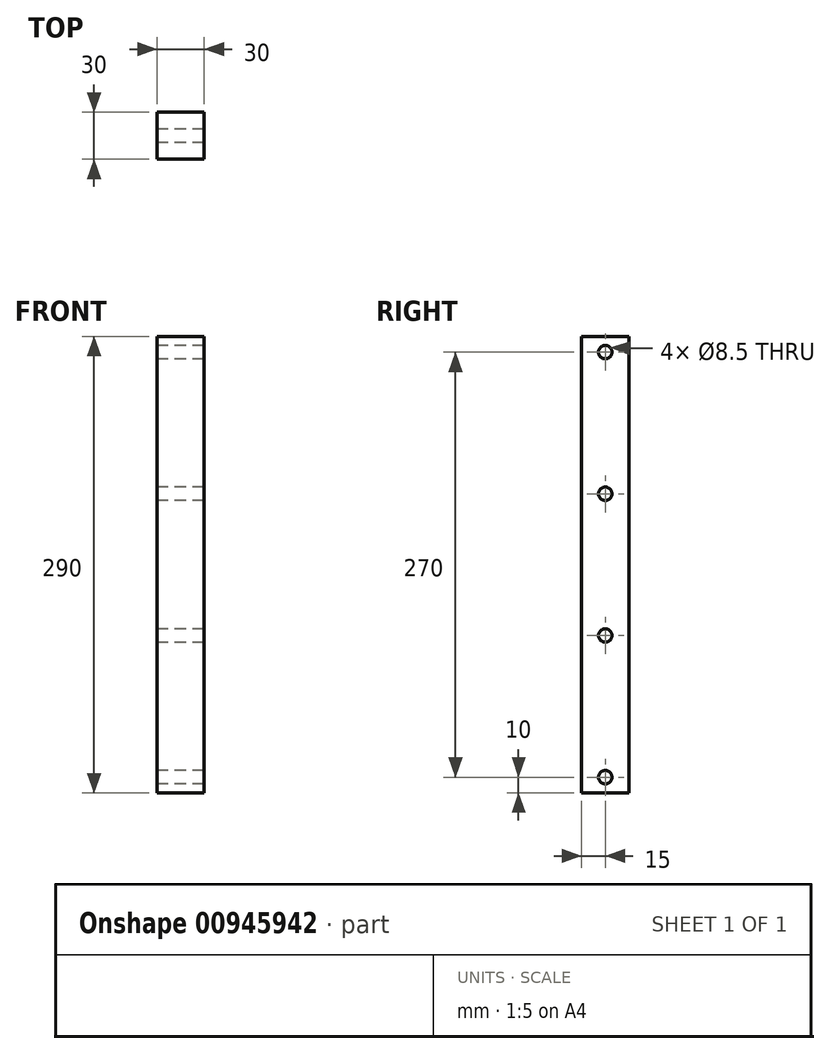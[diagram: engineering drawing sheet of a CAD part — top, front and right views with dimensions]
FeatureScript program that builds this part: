
annotation { "Feature Type Name" : "Feature", "Feature Type Description" : "" }
export const myFeature = defineFeature(function(context is Context, id is Id, definition is map)
    precondition{}
    {
        {
            var Q0;
            Q0=qCreatedBy(makeId("Top.planeOp"),FACE);
            var sketch = newSketch(context, id + "F0", { "sketchPlane" : qUnion([Q0])});
            skLineSegment(sketch, "E0.bottom", {"start": v(15, -15) * mm, "end": v(-15, -15) * mm});
            skLineSegment(sketch, "E0.top", {"start": v(15, 15) * mm, "end": v(-15, 15) * mm});
            skLineSegment(sketch, "E0.left", {"start": v(15, -15) * mm, "end": v(15, 15) * mm});
            skLineSegment(sketch, "E0.right", {"start": v(-15, -15) * mm, "end": v(-15, 15) * mm});
            skPoint(sketch, "E0.middle", {"position": v(0, 0) * mm});
            skSolve(sketch);
        }
        {
            var Q0;
            Q0 = qSketchRegion(id + "F0", true);
            extrude(context, id + "F1", {"entities" : qUnion([Q0]), "depth" : 290 * mm, "offsetDistance" : 25 * mm});
        }
        {
            var Q0;
            Q0=makeQuery(id+"F1.opExtrude","SWEPT_FACE",FACE,{"disambiguationData":[OSD([sQuery(id+"F0.wireOp",EDGE,"E0.right")])]});
            var sketch = newSketch(context, id + "F2", { "sketchPlane" : qUnion([Q0])});
            skLineSegment(sketch, "E1", {"start": v(0, 290) * mm, "end": v(0, 0) * mm, "construction": true});
            skCircle(sketch, "E2", {"center": v(0, 280) * mm, "radius": 4.25 * mm});
            skCircle(sketch, "E3", {"center": v(0, 190) * mm, "radius": 4.25 * mm});
            skCircle(sketch, "E4", {"center": v(0, 100) * mm, "radius": 4.25 * mm});
            skCircle(sketch, "E5", {"center": v(0, 10) * mm, "radius": 4.25 * mm});
            skSolve(sketch);
        }
        {
            var Q0;
            Q0 = qSketchRegion(id + "F2", true);
            extrude(context, id + "F3", {"entities" : qUnion([Q0]), "operationType" : NewBodyOperationType.REMOVE, "endBound" : BoundingType.UP_TO_NEXT, "oppositeDirection" : true, "depth" : 25 * mm, "offsetDistance" : 25 * mm});
        }
    });
